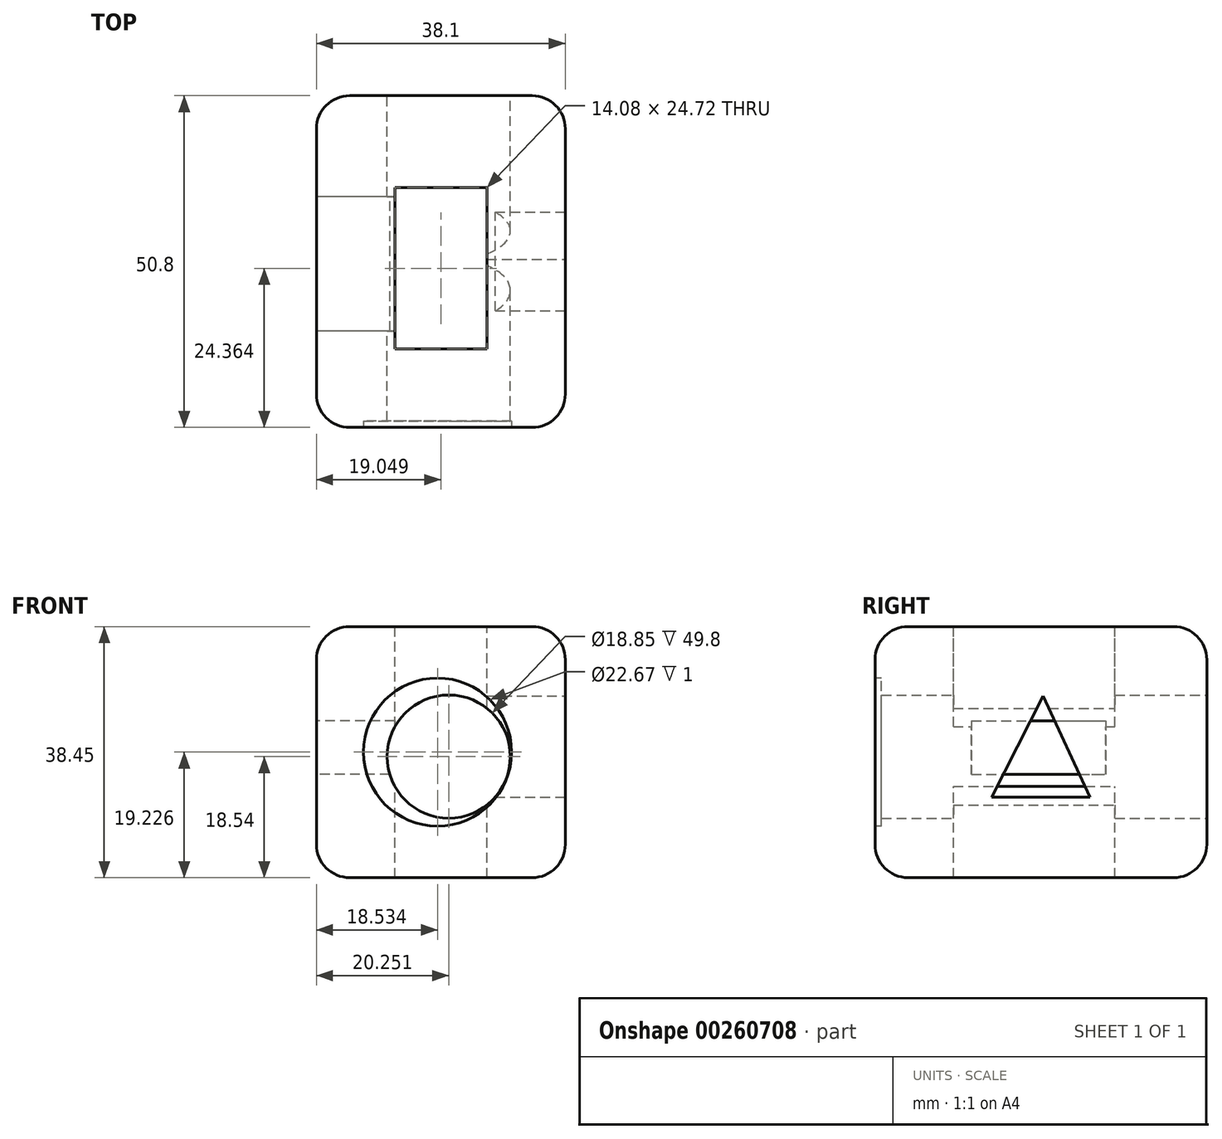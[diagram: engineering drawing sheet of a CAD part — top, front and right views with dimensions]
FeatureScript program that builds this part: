
annotation { "Feature Type Name" : "Feature", "Feature Type Description" : "" }
export const myFeature = defineFeature(function(context is Context, id is Id, definition is map)
    precondition{}
    {
        {
            var Q0;
            Q0=qCreatedBy(makeId("Front.planeOp"),FACE);
            var sketch = newSketch(context, id + "F0", { "sketchPlane" : qUnion([Q0])});
            skLineSegment(sketch, "E0.bottom", {"start": v(-43.94, 29.18) * mm, "end": v(-5.84, 29.18) * mm});
            skLineSegment(sketch, "E0.top", {"start": v(-43.94, -9.27) * mm, "end": v(-5.84, -9.27) * mm});
            skLineSegment(sketch, "E0.left", {"start": v(-43.94, 29.18) * mm, "end": v(-43.94, -9.27) * mm});
            skLineSegment(sketch, "E0.right", {"start": v(-5.84, 29.18) * mm, "end": v(-5.84, -9.27) * mm});
            skSolve(sketch);
        }
        {
            var Q0;
            Q0=makeQuery(id+"F0.imprint","IMPRINT",FACE,{"disambiguationData":[TD([[makeQuery(id+"F0.imprint","IMPRINT",EDGE,{"derivedFrom":sQuery(id+"F0.wireOp",EDGE,"E0.bottom")}),-1.0]])]});
            var sketch = newSketch(context, id + "F1", { "sketchPlane" : qUnion([Q0])});
            skCircle(sketch, "E1", {"center": v(-25.06, 10.99) * mm, "radius": 12.94 * mm});
            skSolve(sketch);
        }
        {
            var Q0;
            Q0=makeQuery(id+"F0.imprint","IMPRINT",FACE,{"disambiguationData":[TD([[makeQuery(id+"F0.imprint","IMPRINT",EDGE,{"derivedFrom":sQuery(id+"F0.wireOp",EDGE,"E0.bottom")}),-1.0]])]});
            extrude(context, id + "F2", {"entities" : qUnion([Q0]), "depth" : 50.8 * mm});
        }
        {
            var Q0;
            Q0=makeQuery(id+"F2.opExtrude","CAP_FACE",FACE,{"disambiguationData":[OSD([sQuery(id+"F0.wireOp",EDGE,"E0.bottom"),sQuery(id+"F0.wireOp",EDGE,"E0.top"),sQuery(id+"F0.wireOp",EDGE,"E0.left"),sQuery(id+"F0.wireOp",EDGE,"E0.right")])],"isStart":false});
            var sketch = newSketch(context, id + "F3", { "sketchPlane" : qUnion([Q0])});
            skCircle(sketch, "E2", {"center": v(-25.4, 9.96) * mm, "radius": 11.33 * mm});
            skSolve(sketch);
        }
        {
            var Q0;
            Q0=makeQuery(id+"F2.opExtrude","CAP_EDGE",EDGE,{"disambiguationData":[OSD([sQuery(id+"F0.wireOp",EDGE,"E0.bottom")])],"isStart":false});
            var Q1;
            Q1=makeQuery(id+"F2.opExtrude","CAP_EDGE",EDGE,{"disambiguationData":[OSD([sQuery(id+"F0.wireOp",EDGE,"E0.left")])],"isStart":false});
            var Q2;
            Q2=makeQuery(id+"F2.opExtrude","CAP_FACE",FACE,{"disambiguationData":[OSD([sQuery(id+"F0.wireOp",EDGE,"E0.bottom"),sQuery(id+"F0.wireOp",EDGE,"E0.top"),sQuery(id+"F0.wireOp",EDGE,"E0.left"),sQuery(id+"F0.wireOp",EDGE,"E0.right")])],"isStart":false});
            fillet(context, id + "F4", {"entities" : qUnion([Q0, Q1, Q2]), "radius" : 5.08 * mm, "tangentPropagation" : true, "allowEdgeOverflow" : false});
        }
        {
            var Q0;
            Q0=makeQuery(id+"F2.opExtrude","CAP_EDGE",EDGE,{"disambiguationData":[OSD([sQuery(id+"F0.wireOp",EDGE,"E0.bottom")])],"isStart":true});
            var Q1;
            Q1=makeQuery(id+"F2.opExtrude","CAP_EDGE",EDGE,{"disambiguationData":[OSD([sQuery(id+"F0.wireOp",EDGE,"E0.right")])],"isStart":true});
            var Q2;
            Q2=makeQuery(id+"F2.opExtrude","CAP_EDGE",EDGE,{"disambiguationData":[OSD([sQuery(id+"F0.wireOp",EDGE,"E0.top")])],"isStart":true});
            var Q3;
            Q3=makeQuery(id+"F2.opExtrude","CAP_EDGE",EDGE,{"disambiguationData":[OSD([sQuery(id+"F0.wireOp",EDGE,"E0.left")])],"isStart":true});
            var Q4;
            Q4=makeQuery(id+"F2.opExtrude","SWEPT_EDGE",EDGE,{"disambiguationData":[OSD([sQuery(id+"F0.wireOp",EDGE,"E0.bottom"),sQuery(id+"F0.wireOp",EDGE,"E0.right")])]});
            var Q5;
            Q5=makeQuery(id+"F2.opExtrude","SWEPT_EDGE",EDGE,{"disambiguationData":[OSD([sQuery(id+"F0.wireOp",EDGE,"E0.top"),sQuery(id+"F0.wireOp",EDGE,"E0.right")])]});
            var Q6;
            Q6=makeQuery(id+"F2.opExtrude","SWEPT_EDGE",EDGE,{"disambiguationData":[OSD([sQuery(id+"F0.wireOp",EDGE,"E0.bottom"),sQuery(id+"F0.wireOp",EDGE,"E0.left")])]});
            var Q7;
            Q7=makeQuery(id+"F2.opExtrude","SWEPT_EDGE",EDGE,{"disambiguationData":[OSD([sQuery(id+"F0.wireOp",EDGE,"E0.top"),sQuery(id+"F0.wireOp",EDGE,"E0.left")])]});
            fillet(context, id + "F5", {"entities" : qUnion([Q0, Q1, Q2, Q3, Q4, Q5, Q6, Q7]), "radius" : 5.08 * mm, "tangentPropagation" : true, "allowEdgeOverflow" : false});
        }
        {
            var Q0;
            Q0=makeQuery(id+"F3.imprint","IMPRINT",FACE,{"disambiguationData":[TD([[makeQuery(id+"F3.imprint","IMPRINT",EDGE,{"derivedFrom":sQuery(id+"F3.wireOp",EDGE,"E2")}),1.0]])]});
            extrude(context, id + "F6", {"entities" : qUnion([Q0]), "operationType" : NewBodyOperationType.REMOVE, "oppositeDirection" : true, "depth" : mm});
        }
        {
            var Q0;
            Q0=makeQuery(id+"F2.opExtrude","SWEPT_FACE",FACE,{"disambiguationData":[OSD([sQuery(id+"F0.wireOp",EDGE,"E0.left")])]});
            var sketch = newSketch(context, id + "F7", { "sketchPlane" : qUnion([Q0])});
            skLineSegment(sketch, "E3.bottom", {"start": v(36.05, 14.76) * mm, "end": v(15.45, 14.76) * mm});
            skLineSegment(sketch, "E3.top", {"start": v(36.05, 6.52) * mm, "end": v(15.45, 6.52) * mm});
            skLineSegment(sketch, "E3.left", {"start": v(36.05, 14.76) * mm, "end": v(36.05, 6.52) * mm});
            skLineSegment(sketch, "E3.right", {"start": v(15.45, 14.76) * mm, "end": v(15.45, 6.52) * mm});
            skSolve(sketch);
        }
        {
            var Q0;
            Q0=makeQuery(id+"F7.imprint","IMPRINT",FACE,{"disambiguationData":[TD([[makeQuery(id+"F7.imprint","IMPRINT",EDGE,{"derivedFrom":sQuery(id+"F7.wireOp",EDGE,"E3.bottom")}),1.0]])]});
            extrude(context, id + "F8", {"entities" : qUnion([Q0]), "operationType" : NewBodyOperationType.REMOVE, "oppositeDirection" : true, "depth" : 12.7 * mm});
        }
        {
            var Q0;
            Q0=makeQuery(id+"F2.opExtrude","SWEPT_FACE",FACE,{"disambiguationData":[OSD([sQuery(id+"F0.wireOp",EDGE,"E0.right")])]});
            var sketch = newSketch(context, id + "F9", { "sketchPlane" : qUnion([Q0])});
            skLineSegment(sketch, "E4", {"start": v(-32.96, 3.09) * mm, "end": v(-17.85, 3.09) * mm});
            skLineSegment(sketch, "E5", {"start": v(-17.85, 3.09) * mm, "end": v(-25.06, 18.54) * mm});
            skLineSegment(sketch, "E6", {"start": v(-25.06, 18.54) * mm, "end": v(-32.96, 3.09) * mm});
            skSolve(sketch);
        }
        {
            var Q0;
            Q0=makeQuery(id+"F9.imprint","IMPRINT",FACE,{"disambiguationData":[TD([[makeQuery(id+"F9.imprint","IMPRINT",EDGE,{"derivedFrom":sQuery(id+"F9.wireOp",EDGE,"E4")}),1.0]])]});
            extrude(context, id + "F10", {"entities" : qUnion([Q0]), "operationType" : NewBodyOperationType.REMOVE, "oppositeDirection" : true, "depth" : 25.4 * mm});
        }
        {
            var Q0;
            Q0=makeQuery(id+"F2.opExtrude","CAP_FACE",FACE,{"disambiguationData":[OSD([sQuery(id+"F0.wireOp",EDGE,"E0.bottom"),sQuery(id+"F0.wireOp",EDGE,"E0.top"),sQuery(id+"F0.wireOp",EDGE,"E0.left"),sQuery(id+"F0.wireOp",EDGE,"E0.right")])],"isStart":true});
            var sketch = newSketch(context, id + "F11", { "sketchPlane" : qUnion([Q0])});
            skCircle(sketch, "E7", {"center": v(23.69, 9.27) * mm, "radius": 9.43 * mm});
            skSolve(sketch);
        }
        {
            var Q0;
            Q0=makeQuery(id+"F11.imprint","IMPRINT",FACE,{"disambiguationData":[TD([[makeQuery(id+"F11.imprint","IMPRINT",EDGE,{"derivedFrom":sQuery(id+"F11.wireOp",EDGE,"E7")}),1.0]])]});
            extrude(context, id + "F12", {"entities" : qUnion([Q0]), "operationType" : NewBodyOperationType.REMOVE, "oppositeDirection" : true, "depth" : 50.8 * mm});
        }
        {
            var Q0;
            Q0=makeQuery(id+"F2.opExtrude","SWEPT_FACE",FACE,{"disambiguationData":[OSD([sQuery(id+"F0.wireOp",EDGE,"E0.bottom")])]});
            var sketch = newSketch(context, id + "F13", { "sketchPlane" : qUnion([Q0])});
            skLineSegment(sketch, "E8.bottom", {"start": v(-17.85, -38.8) * mm, "end": v(-31.93, -38.8) * mm});
            skLineSegment(sketch, "E8.top", {"start": v(-17.85, -14.08) * mm, "end": v(-31.93, -14.08) * mm});
            skLineSegment(sketch, "E8.left", {"start": v(-17.85, -38.8) * mm, "end": v(-17.85, -14.08) * mm});
            skLineSegment(sketch, "E8.right", {"start": v(-31.93, -38.8) * mm, "end": v(-31.93, -14.08) * mm});
            skSolve(sketch);
        }
        {
            var Q0;
            Q0=makeQuery(id+"F13.imprint","IMPRINT",FACE,{"disambiguationData":[TD([[makeQuery(id+"F13.imprint","IMPRINT",EDGE,{"derivedFrom":sQuery(id+"F13.wireOp",EDGE,"E8.bottom")}),-1.0]])]});
            extrude(context, id + "F14", {"entities" : qUnion([Q0]), "operationType" : NewBodyOperationType.REMOVE, "oppositeDirection" : true, "depth" : 50.8 * mm});
        }
    });
